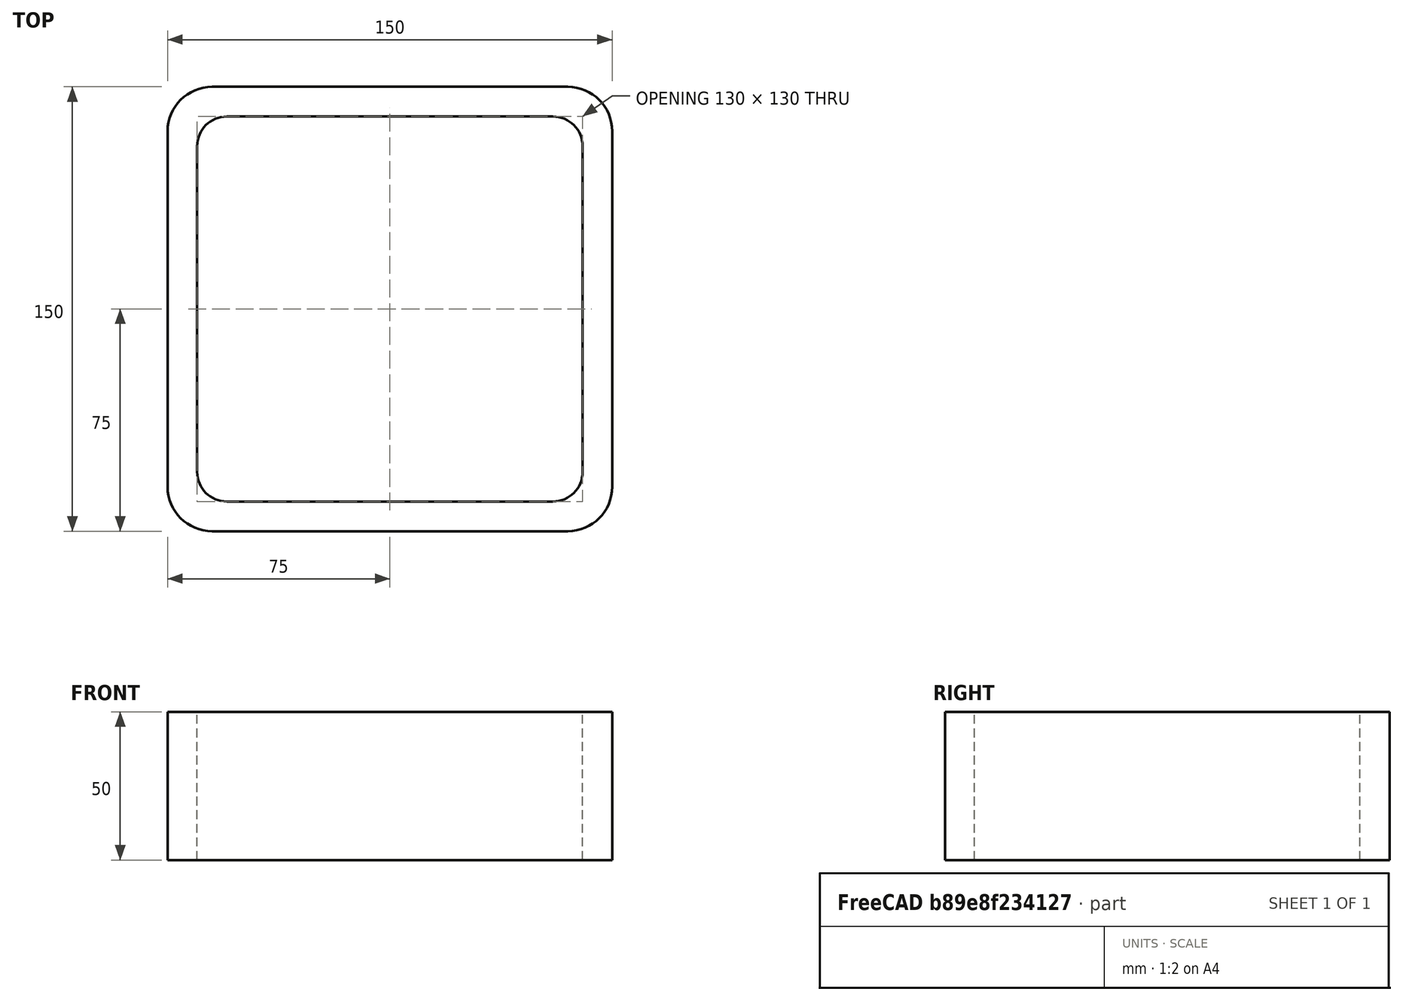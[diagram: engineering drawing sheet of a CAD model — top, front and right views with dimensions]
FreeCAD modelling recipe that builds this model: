
FCSTD DOCUMENT  (FreeCAD 0.15R4671 (Git))
Label: Square hollow section 150x150x10 EN10219 S235JRH
License: All rights reserved
LicenseURL: http://en.wikipedia.org/wiki/All_rights_reserved
objects: Sketcher::SketchObject×1, Part::Extrusion×1
note: 2 computed .brp shape members not serialized (recipe doc carries the construction recipe); baked Part::Feature solids carry a one-line shape summary decoded from their .brp

FEATURE [Sketcher::SketchObject] Sketch
  sketch-geometry (16):
    g0: LineSegment StartX=-55 StartY=65 StartZ=0 EndX=55 EndY=65 EndZ=0
    g1: LineSegment StartX=65 StartY=55 StartZ=0 EndX=65 EndY=-55 EndZ=0
    g2: LineSegment StartX=55 StartY=-65 StartZ=0 EndX=-55 EndY=-65 EndZ=0
    g3: LineSegment StartX=-65 StartY=-55 StartZ=0 EndX=-65 EndY=55 EndZ=0
    g4: LineSegment StartX=-60 StartY=75 StartZ=0 EndX=60 EndY=75 EndZ=0
    g5: LineSegment StartX=75 StartY=60 StartZ=0 EndX=75 EndY=-60 EndZ=0
    g6: LineSegment StartX=60 StartY=-75 StartZ=0 EndX=-60 EndY=-75 EndZ=0
    g7: LineSegment StartX=-75 StartY=-60 StartZ=0 EndX=-75 EndY=60 EndZ=0
    g8: ArcOfCircle CenterX=-55 CenterY=55 CenterZ=0 NormalX=0 NormalY=0 NormalZ=1 Radius=10 StartAngle=1.5708 EndAngle=3.14159
    g9: ArcOfCircle CenterX=55 CenterY=55 CenterZ=0 NormalX=0 NormalY=0 NormalZ=1 Radius=10 StartAngle=0 EndAngle=1.5708
    g10: ArcOfCircle CenterX=55 CenterY=-55 CenterZ=0 NormalX=0 NormalY=0 NormalZ=1 Radius=10 StartAngle=4.71239 EndAngle=6.28319
    g11: ArcOfCircle CenterX=-55 CenterY=-55 CenterZ=0 NormalX=0 NormalY=0 NormalZ=1 Radius=10 StartAngle=3.14159 EndAngle=4.71239
    g12: ArcOfCircle CenterX=60 CenterY=60 CenterZ=0 NormalX=0 NormalY=0 NormalZ=1 Radius=15 StartAngle=0 EndAngle=1.5708
    g13: ArcOfCircle CenterX=60 CenterY=-60 CenterZ=0 NormalX=0 NormalY=0 NormalZ=1 Radius=15 StartAngle=4.71239 EndAngle=6.28319
    g14: ArcOfCircle CenterX=-60 CenterY=-60 CenterZ=0 NormalX=0 NormalY=0 NormalZ=1 Radius=15 StartAngle=3.14159 EndAngle=4.71239
    g15: ArcOfCircle CenterX=-60 CenterY=60 CenterZ=0 NormalX=0 NormalY=0 NormalZ=1 Radius=15 StartAngle=1.5708 EndAngle=3.14159
  constraints (36):
    c: Horizontal(g2)
    c: Vertical(g3)
    c: Horizontal(g6)
    c: Vertical(g7)
    c: Tangent(g3,g8) = 1.5708
    c: Tangent(g0,g8) = 1.5708
    c: Tangent(g0,g9) = 1.5708
    c: Tangent(g1,g9) = 1.5708
    c: Tangent(g1,g10) = 1.5708
    c: Tangent(g2,g10) = 1.5708
    c: Tangent(g2,g11) = 1.5708
    c: Tangent(g3,g11) = 1.5708
    c: Tangent(g4,g12) = 1.5708
    c: Tangent(g5,g12) = 1.5708
    c: Tangent(g5,g13) = 1.5708
    c: Tangent(g6,g13) = 1.5708
    c: Tangent(g6,g14) = 1.5708
    c: Tangent(g7,g14) = 1.5708
    c: Tangent(g7,g15) = 1.5708
    c: Tangent(g4,g15) = 1.5708
    c: Equal(g9,g8)
    c: Equal(g9,g11)
    c: Equal(g9,g10)
    c: Equal(g12,g15)
    c: Equal(g12,g14)
    c: Equal(g12,g13)
    c: Symmetric(g4,g6,g-1)
    c: Symmetric(g7,g5,g-2)
    c: DistanceY(g4,g6) = -150
    c: DistanceX(g7,g5) = 150
    c: Symmetric(g3,g1,g-2)
    c: Symmetric(g0,g2,g-1)
    c: DistanceY(g0,g4) = 10
    c: DistanceX(g5,g1) = -10
    c: Radius(g9) = 10
    c: Radius(g12) = 15
FEATURE [Part::Extrusion] Extrude  label="Square hollow section 150x150x10 EN10219 S235JRH"
  Base = -> Sketch
  Dir = (0,0,50)
  Solid = true
